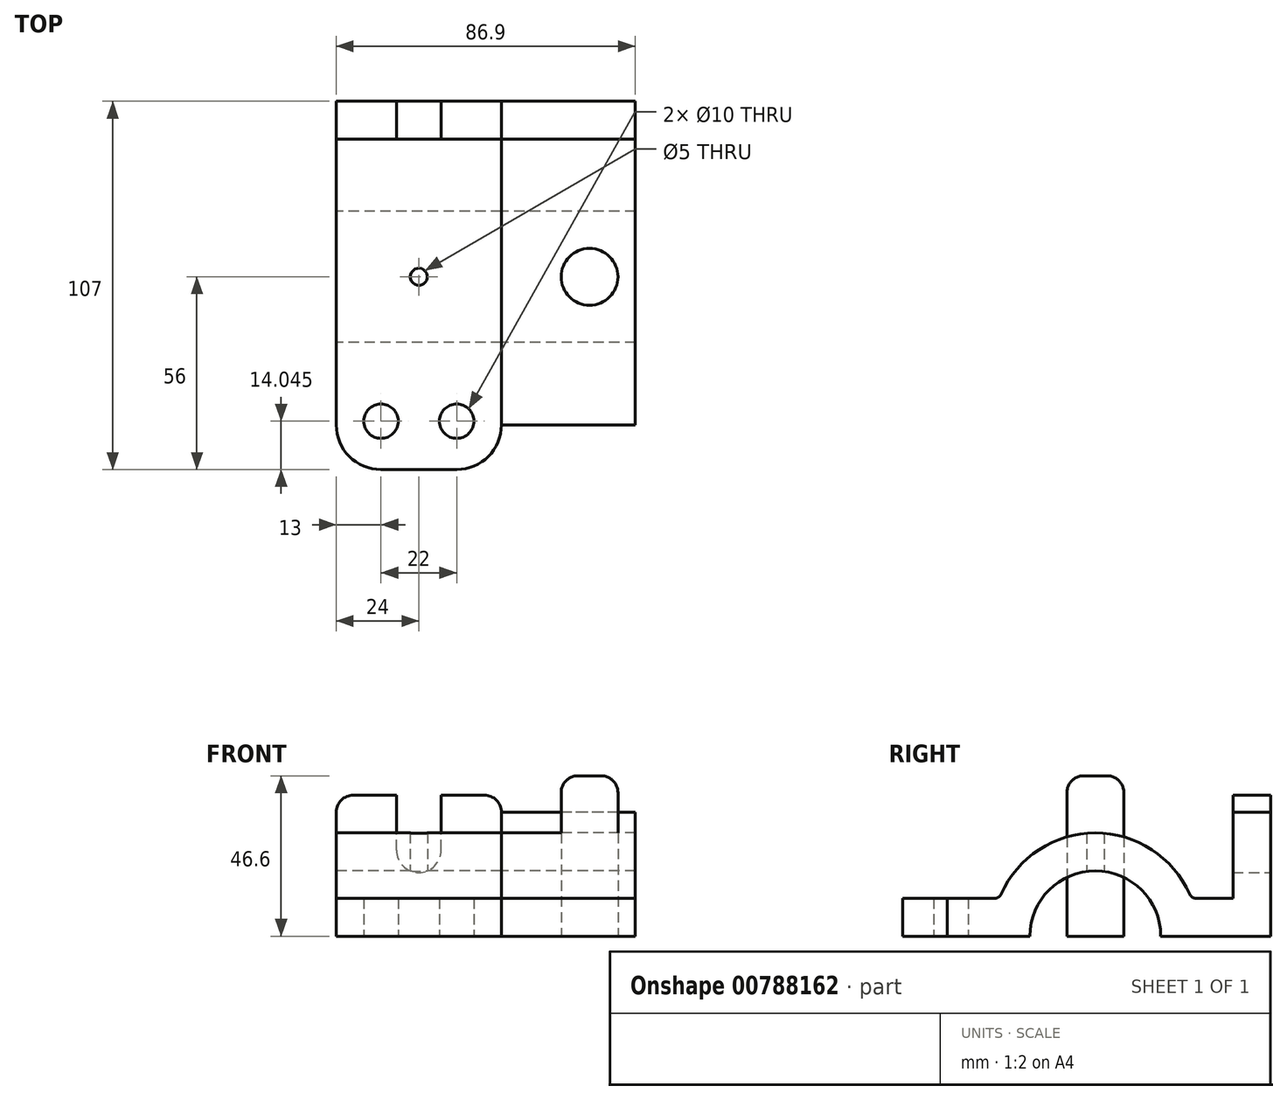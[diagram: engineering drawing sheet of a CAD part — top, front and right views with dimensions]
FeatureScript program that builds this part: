
annotation { "Feature Type Name" : "Feature", "Feature Type Description" : "" }
export const myFeature = defineFeature(function(context is Context, id is Id, definition is map)
    precondition{}
    {
        {
            var Q0;
            Q0=qCreatedBy(makeId("Right.planeOp"),FACE);
            var sketch = newSketch(context, id + "F0", { "sketchPlane" : qUnion([Q0])});
            skCircle(sketch, "E0", {"center": v(0, 0) * mm, "radius": 19 * mm});
            skCircle(sketch, "E1", {"center": v(0, 0) * mm, "radius": 30 * mm});
            skLineSegment(sketch, "E2.bottom", {"start": v(-56, 0) * mm, "end": v(51, 0) * mm});
            skLineSegment(sketch, "E2.top", {"start": v(-56, 11) * mm, "end": v(51, 11) * mm});
            skLineSegment(sketch, "E2.left", {"start": v(-56, 0) * mm, "end": v(-56, 11) * mm});
            skLineSegment(sketch, "E2.right", {"start": v(51, 0) * mm, "end": v(51, 11) * mm});
            skLineSegment(sketch, "E3.bottom", {"start": v(51, 11) * mm, "end": v(40, 11) * mm});
            skLineSegment(sketch, "E3.top", {"start": v(51, 41) * mm, "end": v(40, 41) * mm});
            skLineSegment(sketch, "E3.left", {"start": v(51, 11) * mm, "end": v(51, 41) * mm});
            skLineSegment(sketch, "E3.right", {"start": v(40, 11) * mm, "end": v(40, 41) * mm});
            skSolve(sketch);
        }
        {
            var Q0;
            {var subQ5=sQuery(id+"F0.wireOp",EDGE,"E2.left");Q0=makeQuery(id+"F0.imprint","IMPRINT",FACE,{"disambiguationData":[TD([[makeQuery(id+"F0.imprint","IMPRINT",EDGE,{"derivedFrom":subQ5}),-1.0]])]});}
            var Q1;
            {var subQ0=sQuery(id+"F0.wireOp",EDGE,"E2.bottom");var subQ1=sQuery(id+"F0.wireOp",EDGE,"E0");var subQ2=makeQuery(id+"F0.imprint","INTERSECT",VERTEX,{"disambiguationData":[OD(0.0)],"derivedFrom":[subQ1,subQ0]});Q1=makeQuery(id+"F0.imprint","IMPRINT",FACE,{"disambiguationData":[TD([[makeQuery(id+"F0.imprint","IMPRINT",EDGE,{"disambiguationData":[TD([[subQ2,1.0]])],"derivedFrom":subQ1}),-1.0]])]});}
            var Q2;
            {var subQ0=sQuery(id+"F0.wireOp",EDGE,"E2.top");var subQ1=sQuery(id+"F0.wireOp",EDGE,"E0");var subQ2=makeQuery(id+"F0.imprint","INTERSECT",VERTEX,{"disambiguationData":[OD(0.0)],"derivedFrom":[subQ1,subQ0]});Q2=makeQuery(id+"F0.imprint","IMPRINT",FACE,{"disambiguationData":[TD([[makeQuery(id+"F0.imprint","IMPRINT",EDGE,{"disambiguationData":[TD([[subQ2,1.0]])],"derivedFrom":subQ1}),-1.0]])]});}
            var Q3;
            {var subQ0=sQuery(id+"F0.wireOp",EDGE,"E2.top");var subQ1=sQuery(id+"F0.wireOp",EDGE,"E0");var subQ2=makeQuery(id+"F0.imprint","INTERSECT",VERTEX,{"disambiguationData":[OD(1.0)],"derivedFrom":[subQ1,subQ0]});Q3=makeQuery(id+"F0.imprint","IMPRINT",FACE,{"disambiguationData":[TD([[makeQuery(id+"F0.imprint","IMPRINT",EDGE,{"disambiguationData":[TD([[subQ2,1.0]])],"derivedFrom":subQ1}),-1.0]])]});}
            var Q4;
            {var subQ0=sQuery(id+"F0.wireOp",EDGE,"E2.right");Q4=makeQuery(id+"F0.imprint","IMPRINT",FACE,{"disambiguationData":[TD([[makeQuery(id+"F0.imprint","IMPRINT",EDGE,{"derivedFrom":subQ0}),1.0]])]});}
            var Q5;
            Q5=makeQuery(id+"F0.imprint","IMPRINT",FACE,{"disambiguationData":[TD([[makeQuery(id+"F0.imprint","IMPRINT",EDGE,{"derivedFrom":sQuery(id+"F0.wireOp",EDGE,"E3.top")}),1.0]])]});
            extrude(context, id + "F1", {"entities" : qUnion([Q0, Q1, Q2, Q3, Q4, Q5]), "endBound" : BoundingType.SYMMETRIC, "depth" : 48 * mm});
        }
        {
            var Q0;
            Q0=makeQuery(id+"F1.opExtrude","SWEPT_FACE",FACE,{"disambiguationData":[OSD([sQuery(id+"F0.wireOp",EDGE,"E2.right"),sQuery(id+"F0.wireOp",EDGE,"E3.left")])]});
            var sketch = newSketch(context, id + "F2", { "sketchPlane" : qUnion([Q0])});
            skLineSegment(sketch, "E4", {"start": v(0, 0) * mm, "end": v(0, 41) * mm, "construction": true});
            skCircle(sketch, "E5", {"center": v(0, 25) * mm, "radius": 6.5 * mm});
            skLineSegment(sketch, "E6", {"start": v(-6.5, 25) * mm, "end": v(-6.5, 41) * mm});
            skLineSegment(sketch, "E7", {"start": v(6.5, 25) * mm, "end": v(6.5, 41) * mm});
            skSolve(sketch);
        }
        {
            var Q0;
            {var subQ0=sQuery(id+"F2.wireOp",EDGE,"E5");var subQ2=makeQuery(id+"F2.imprint","INTERSECT",VERTEX,{"derivedFrom":[subQ0,sQuery(id+"F2.wireOp",EDGE,"E6")]});Q0=makeQuery(id+"F2.imprint","IMPRINT",FACE,{"disambiguationData":[TD([[makeQuery(id+"F2.imprint","IMPRINT",EDGE,{"disambiguationData":[TD([[subQ2,1.0]])],"derivedFrom":subQ0}),1.0]])]});}
            var Q1;
            {var subQ2=sQuery(id+"F2.wireOp",EDGE,"E6");Q1=makeQuery(id+"F2.imprint","IMPRINT",FACE,{"disambiguationData":[TD([[makeQuery(id+"F2.imprint","IMPRINT",EDGE,{"derivedFrom":subQ2}),-1.0]])]});}
            var Q2;
            Q2=makeQuery(id+"F1.opExtrude","SWEPT_FACE",FACE,{"disambiguationData":[OSD([sQuery(id+"F0.wireOp",EDGE,"E3.right")])]});
            extrude(context, id + "F3", {"entities" : qUnion([Q0, Q1]), "operationType" : NewBodyOperationType.REMOVE, "endBound" : BoundingType.UP_TO_SURFACE, "oppositeDirection" : true, "endBoundEntityFace" : qUnion([Q2]), "depth" : 25 * mm});
        }
        {
            var Q0;
            Q0=qCreatedBy(makeId("Top.planeOp"),FACE);
            var sketch = newSketch(context, id + "F4", { "sketchPlane" : qUnion([Q0])});
            skCircle(sketch, "E8", {"center": v(0, 0) * mm, "radius": 2.5 * mm});
            skLineSegment(sketch, "E9", {"start": v(24, -41.96) * mm, "end": v(-24, -41.96) * mm, "construction": true});
            skLineSegment(sketch, "E10", {"start": v(0, -56) * mm, "end": v(0, -27.91) * mm, "construction": true});
            skCircle(sketch, "E11", {"center": v(-11, -41.96) * mm, "radius": 5 * mm});
            skCircle(sketch, "E12", {"center": v(11, -41.96) * mm, "radius": 5 * mm});
            skSolve(sketch);
        }
        {
            var Q0;
            Q0=qSketchRegion(id+"F4",true);
            extrude(context, id + "F5", {"entities" : qUnion([Q0]), "operationType" : NewBodyOperationType.REMOVE, "endBound" : BoundingType.THROUGH_ALL, "depth" : 25 * mm});
        }
        {
            var Q0;
            Q0=makeQuery(id+"F1.opExtrude","CAP_EDGE",EDGE,{"disambiguationData":[OSD([sQuery(id+"F0.wireOp",EDGE,"E2.left")])],"isStart":false});
            var Q1;
            Q1=makeQuery(id+"F1.opExtrude","CAP_EDGE",EDGE,{"disambiguationData":[OSD([sQuery(id+"F0.wireOp",EDGE,"E2.left")])],"isStart":true});
            fillet(context, id + "F6", {"entities" : qUnion([Q0, Q1]), "radius" : 13 * mm, "tangentPropagation" : true, "allowEdgeOverflow" : false});
        }
        {
            var Q0;
            Q0=makeQuery(id+"F1.opExtrude","CAP_EDGE",EDGE,{"disambiguationData":[OSD([sQuery(id+"F0.wireOp",EDGE,"E3.top")])],"isStart":false});
            var Q1;
            Q1=makeQuery(id+"F1.opExtrude","CAP_EDGE",EDGE,{"disambiguationData":[OSD([sQuery(id+"F0.wireOp",EDGE,"E3.top")])],"isStart":true});
            fillet(context, id + "F7", {"entities" : qUnion([Q0, Q1]), "radius" : 5 * mm, "tangentPropagation" : true, "allowEdgeOverflow" : false});
        }
        {
            var Q0;
            {var subQ0=sQuery(id+"F0.wireOp",EDGE,"E2.top");var subQ1=sQuery(id+"F0.wireOp",EDGE,"E1");Q0=makeQuery(id+"F1.opExtrude","SWEPT_EDGE",EDGE,{"disambiguationData":[OSD([subQ1,subQ0]),TDD([makeQuery(id+"F0.imprint","INTERSECT",VERTEX,{"disambiguationData":[OD(1.0)],"derivedFrom":[subQ1,subQ0]})])]});}
            var Q1;
            {var subQ0=sQuery(id+"F0.wireOp",EDGE,"E2.top");var subQ1=sQuery(id+"F0.wireOp",EDGE,"E1");Q1=makeQuery(id+"F1.opExtrude","SWEPT_EDGE",EDGE,{"disambiguationData":[OSD([subQ1,subQ0]),TDD([makeQuery(id+"F0.imprint","INTERSECT",VERTEX,{"disambiguationData":[OD(0.0)],"derivedFrom":[subQ1,subQ0]})])]});}
            fillet(context, id + "F8", {"entities" : qUnion([Q0, Q1]), "radius" : 2 * mm, "tangentPropagation" : true, "allowEdgeOverflow" : false});
        }
        {
            var Q0;
            Q0=qCreatedBy(makeId("Top.planeOp"),FACE);
            var sketch = newSketch(context, id + "F9", { "sketchPlane" : qUnion([Q0])});
            skCircle(sketch, "E13", {"center": v(49.6, 0) * mm, "radius": 8.26 * mm});
            skSolve(sketch);
        }
        {
            var Q0;
            Q0=makeQuery(id+"F9.imprint","IMPRINT",FACE,{"disambiguationData":[TD([[makeQuery(id+"F9.imprint","IMPRINT",EDGE,{"derivedFrom":sQuery(id+"F9.wireOp",EDGE,"E13")}),1.0]])]});
            extrude(context, id + "F10", {"entities" : qUnion([Q0]), "depth" : 46.6 * mm, "offsetDistance" : 25 * mm});
        }
        {
            var Q0;
            Q0=makeQuery(id+"F10.opExtrude","CAP_EDGE",EDGE,{"disambiguationData":[OSD([sQuery(id+"F9.wireOp",EDGE,"E13")])],"isStart":false});
            fillet(context, id + "F11", {"entities" : qUnion([Q0]), "radius" : 4.83 * mm, "tangentPropagation" : true, "allowEdgeOverflow" : false});
        }
        {
            var Q0;
            Q0=makeQuery(id+"F1.opExtrude","CAP_FACE",FACE,{"disambiguationData":[OSD([sQuery(id+"F0.wireOp",EDGE,"E0"),sQuery(id+"F0.wireOp",EDGE,"E1"),sQuery(id+"F0.wireOp",EDGE,"E2.bottom"),sQuery(id+"F0.wireOp",EDGE,"E2.top"),sQuery(id+"F0.wireOp",EDGE,"E2.left"),sQuery(id+"F0.wireOp",EDGE,"E2.right"),sQuery(id+"F0.wireOp",EDGE,"E3.top"),sQuery(id+"F0.wireOp",EDGE,"E3.left"),sQuery(id+"F0.wireOp",EDGE,"E3.right")])],"isStart":false});
            extrude(context, id + "F12", {"entities" : qUnion([Q0]), "depth" : 38.9 * mm, "offsetDistance" : 25 * mm});
        }
    });
